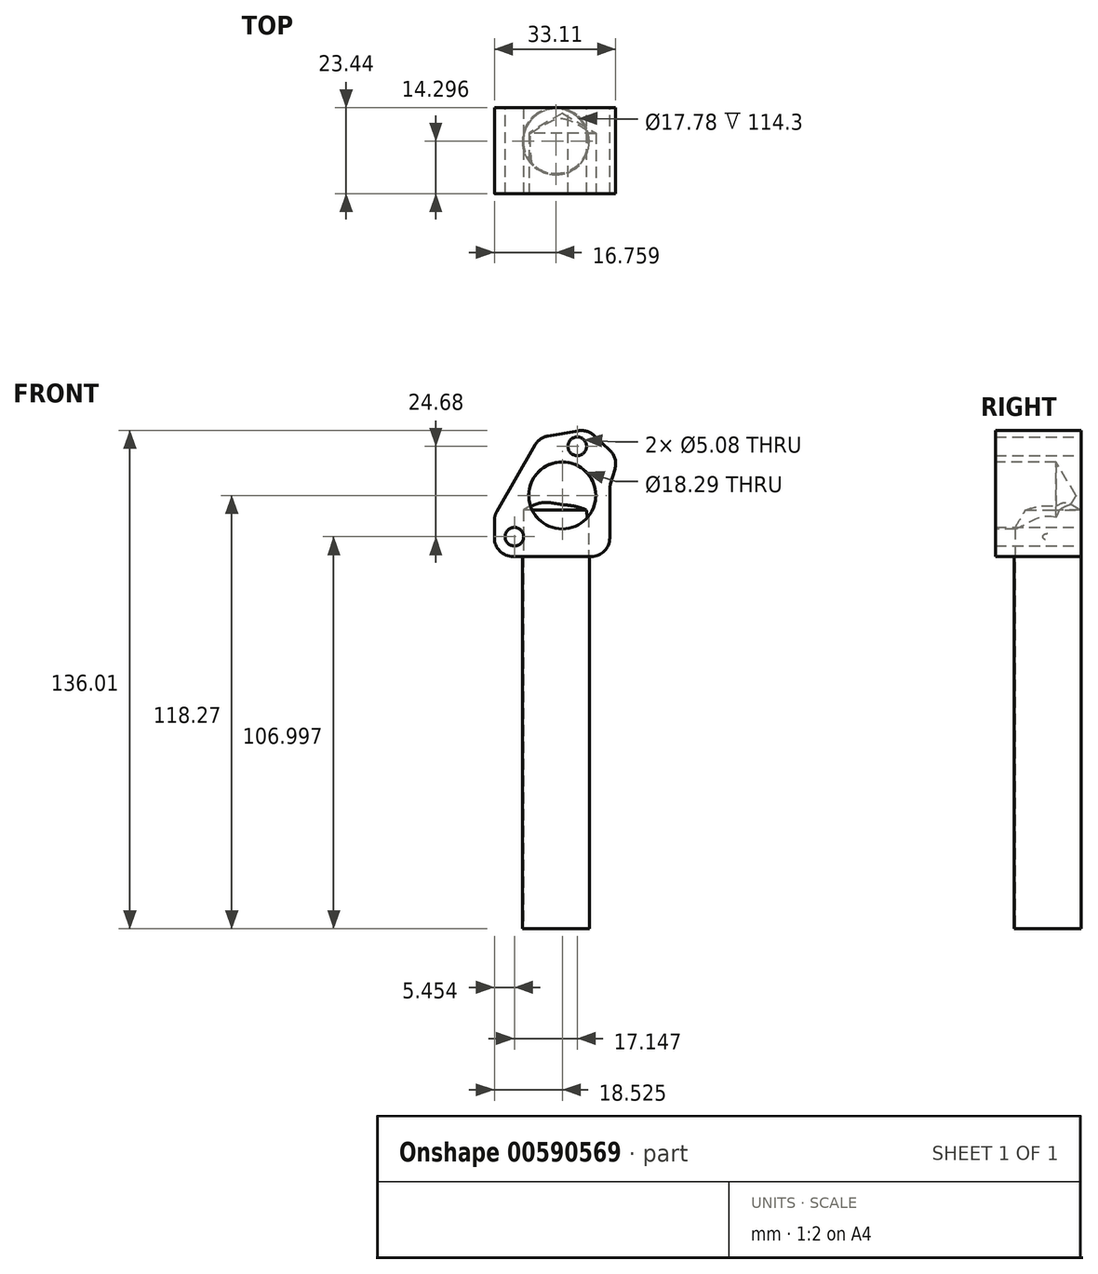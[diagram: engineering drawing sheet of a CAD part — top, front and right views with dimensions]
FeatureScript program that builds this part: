
annotation { "Feature Type Name" : "Feature", "Feature Type Description" : "" }
export const myFeature = defineFeature(function(context is Context, id is Id, definition is map)
    precondition{}
    {
        {
            var Q0;
            Q0=qCreatedBy(makeId("Front.planeOp"),FACE);
            var sketch = newSketch(context, id + "F0", { "sketchPlane" : qUnion([Q0])});
            skCircle(sketch, "E0", {"center": v(-13.8, 25.53) * mm, "radius": 2.54 * mm});
            skCircle(sketch, "E1", {"center": v(3.34, 50.2) * mm, "radius": 2.54 * mm});
            skLineSegment(sketch, "E2", {"start": v(6.1, 54.9) * mm, "end": v(-6.94, 52.64) * mm});
            skLineSegment(sketch, "E3", {"start": v(-6.94, 52.64) * mm, "end": v(-19.26, 31.3) * mm});
            skLineSegment(sketch, "E4", {"start": v(-19.26, 31.3) * mm, "end": v(-19.26, 20.13) * mm});
            skLineSegment(sketch, "E5", {"start": v(-19.26, 20.13) * mm, "end": v(12.24, 20.13) * mm});
            skLineSegment(sketch, "E6", {"start": v(12.24, 20.13) * mm, "end": v(12.24, 39.18) * mm});
            skLineSegment(sketch, "E7", {"start": v(12.24, 39.18) * mm, "end": v(14.51, 46.98) * mm});
            skLineSegment(sketch, "E8", {"start": v(14.51, 46.98) * mm, "end": v(6.1, 54.9) * mm});
            skLineSegment(sketch, "E9", {"start": v(12.24, 20.13) * mm, "end": v(0.66, 20.13) * mm});
            skPoint(sketch, "E10.third.point", {"position": v(-6.58, 29.77) * mm});
            skSolve(sketch);
        }
        {
            var Q0;
            Q0=makeQuery(id+"F0.imprint","IMPRINT",FACE,{"disambiguationData":[TD([[makeQuery(id+"F0.imprint","IMPRINT",EDGE,{"derivedFrom":sQuery(id+"F0.wireOp",EDGE,"E0")}),-1.0]])]});
            extrude(context, id + "F1", {"entities" : qUnion([Q0]), "depth" : 23.44 * mm, "offsetDistance" : 25.4 * mm});
        }
        {
            var Q0;
            Q0=makeQuery(id+"F1.opExtrude","CAP_FACE",FACE,{"disambiguationData":[OSD([sQuery(id+"F0.wireOp",EDGE,"E0"),sQuery(id+"F0.wireOp",EDGE,"E1"),sQuery(id+"F0.wireOp",EDGE,"E2"),sQuery(id+"F0.wireOp",EDGE,"E3"),sQuery(id+"F0.wireOp",EDGE,"E4"),sQuery(id+"F0.wireOp",EDGE,"E5"),sQuery(id+"F0.wireOp",EDGE,"E6"),sQuery(id+"F0.wireOp",EDGE,"E7"),sQuery(id+"F0.wireOp",EDGE,"E8"),sQuery(id+"F0.wireOp",EDGE,"E9"),sQuery(id+"F0.wireOp",EDGE,"E10")])],"isStart":false});
            var sketch = newSketch(context, id + "F2", { "sketchPlane" : qUnion([Q0])});
            skCircle(sketch, "E11", {"center": v(-0.73, 36.8) * mm, "radius": 9.14 * mm});
            skPoint(sketch, "E11.first.point", {"position": v(2.59, 45.32) * mm});
            skPoint(sketch, "E11.second.point", {"position": v(-6.67, 29.85) * mm});
            skPoint(sketch, "E11.third.point", {"position": v(5.35, 29.97) * mm});
            skSolve(sketch);
        }
        {
            var Q0;
            Q0=sQuery(id+"F2.wireOp",VERTEX,"E11.center");
            var Q1;
            Q1=makeQuery(id+"F1.opExtrude","SWEPT_BODY",BODY,{"disambiguationData":[OSD([sQuery(id+"F0.wireOp",EDGE,"E0"),sQuery(id+"F0.wireOp",EDGE,"E1"),sQuery(id+"F0.wireOp",EDGE,"E2"),sQuery(id+"F0.wireOp",EDGE,"E3"),sQuery(id+"F0.wireOp",EDGE,"E4"),sQuery(id+"F0.wireOp",EDGE,"E5"),sQuery(id+"F0.wireOp",EDGE,"E6"),sQuery(id+"F0.wireOp",EDGE,"E7"),sQuery(id+"F0.wireOp",EDGE,"E8"),sQuery(id+"F0.wireOp",EDGE,"E9")])]});
            hole(context, id + "F3", {"style" : HoleStyle.SIMPLE, "endStyle" : HoleEndStyle.BLIND, "holeDiameter" : 18.29 * mm, "majorDiameter" : 6.35 * mm, "holeDepth" : 16.5 * mm, "isTappedThrough" : true, "tappedDepth" : 12.7 * mm, "tapClearance" : 3, "locations" : qUnion([Q0]), "scope" : qUnion([Q1])});
        }
        {
            var Q0;
            Q0=makeQuery(id+"F1.opExtrude","SWEPT_FACE",FACE,{"disambiguationData":[OSD([sQuery(id+"F0.wireOp",EDGE,"E5"),sQuery(id+"F0.wireOp",EDGE,"E9")])]});
            var sketch = newSketch(context, id + "F4", { "sketchPlane" : qUnion([Q0])});
            skPoint(sketch, "E12.third.point", {"position": v(0, 0) * mm});
            skCircle(sketch, "E13", {"center": v(-2.5, 9.14) * mm, "radius": 9.14 * mm});
            skSolve(sketch);
        }
        {
            var Q0;
            Q0=makeQuery(id+"F4.imprint","IMPRINT",FACE,{"disambiguationData":[TD([[makeQuery(id+"F4.imprint","IMPRINT",EDGE,{"derivedFrom":sQuery(id+"F4.wireOp",EDGE,"E13")}),1.0]])]});
            extrude(context, id + "F5", {"entities" : qUnion([Q0]), "operationType" : NewBodyOperationType.ADD, "depth" : 101.6 * mm, "offsetDistance" : 25.4 * mm});
        }
        {
            var Q0;
            Q0=makeQuery(id+"F5.opExtrude","CAP_FACE",FACE,{"disambiguationData":[OSD([sQuery(id+"F4.wireOp",EDGE,"E13")])],"isStart":false});
            var sketch = newSketch(context, id + "F6", { "sketchPlane" : qUnion([Q0])});
            skCircle(sketch, "E14", {"center": v(-2.5, 9.14) * mm, "radius": 8.88 * mm});
            skSolve(sketch);
        }
        {
            var Q0;
            Q0=sQuery(id+"F6.wireOp",VERTEX,"E14.center");
            var Q1;
            Q1=makeQuery(id+"F1.opExtrude","SWEPT_BODY",BODY,{"disambiguationData":[OSD([sQuery(id+"F0.wireOp",EDGE,"E0"),sQuery(id+"F0.wireOp",EDGE,"E1"),sQuery(id+"F0.wireOp",EDGE,"E2"),sQuery(id+"F0.wireOp",EDGE,"E3"),sQuery(id+"F0.wireOp",EDGE,"E4"),sQuery(id+"F0.wireOp",EDGE,"E5"),sQuery(id+"F0.wireOp",EDGE,"E6"),sQuery(id+"F0.wireOp",EDGE,"E7"),sQuery(id+"F0.wireOp",EDGE,"E8"),sQuery(id+"F0.wireOp",EDGE,"E9")])]});
            hole(context, id + "F7", {"style" : HoleStyle.SIMPLE, "endStyle" : HoleEndStyle.BLIND, "holeDiameter" : 17.78 * mm, "majorDiameter" : 6.35 * mm, "holeDepth" : 114.3 * mm, "isTappedThrough" : true, "tappedDepth" : 12.7 * mm, "tapClearance" : 3, "locations" : qUnion([Q0]), "scope" : qUnion([Q1])});
        }
        {
            var Q0;
            Q0=makeQuery(id+"F1.opExtrude","SWEPT_EDGE",EDGE,{"disambiguationData":[OSD([sQuery(id+"F0.wireOp",EDGE,"E2"),sQuery(id+"F0.wireOp",EDGE,"E8")])]});
            var Q1;
            Q1=makeQuery(id+"F1.opExtrude","SWEPT_EDGE",EDGE,{"disambiguationData":[OSD([sQuery(id+"F0.wireOp",EDGE,"E7"),sQuery(id+"F0.wireOp",EDGE,"E8")])]});
            var Q2;
            Q2=makeQuery(id+"F1.opExtrude","SWEPT_EDGE",EDGE,{"disambiguationData":[OSD([sQuery(id+"F0.wireOp",EDGE,"E6"),sQuery(id+"F0.wireOp",EDGE,"E9")])]});
            var Q3;
            Q3=makeQuery(id+"F1.opExtrude","SWEPT_EDGE",EDGE,{"disambiguationData":[OSD([sQuery(id+"F0.wireOp",EDGE,"E4"),sQuery(id+"F0.wireOp",EDGE,"E5")])]});
            var Q4;
            Q4=makeQuery(id+"F1.opExtrude","SWEPT_EDGE",EDGE,{"disambiguationData":[OSD([sQuery(id+"F0.wireOp",EDGE,"E2"),sQuery(id+"F0.wireOp",EDGE,"E3")])]});
            var Q5;
            Q5=makeQuery(id+"F1.opExtrude","SWEPT_EDGE",EDGE,{"disambiguationData":[OSD([sQuery(id+"F0.wireOp",EDGE,"E3"),sQuery(id+"F0.wireOp",EDGE,"E4")])]});
            fillet(context, id + "F8", {"entities" : qUnion([Q0, Q1, Q2, Q3, Q4, Q5]), "radius" : 5.08 * mm, "tangentPropagation" : true, "allowEdgeOverflow" : false});
        }
    });
